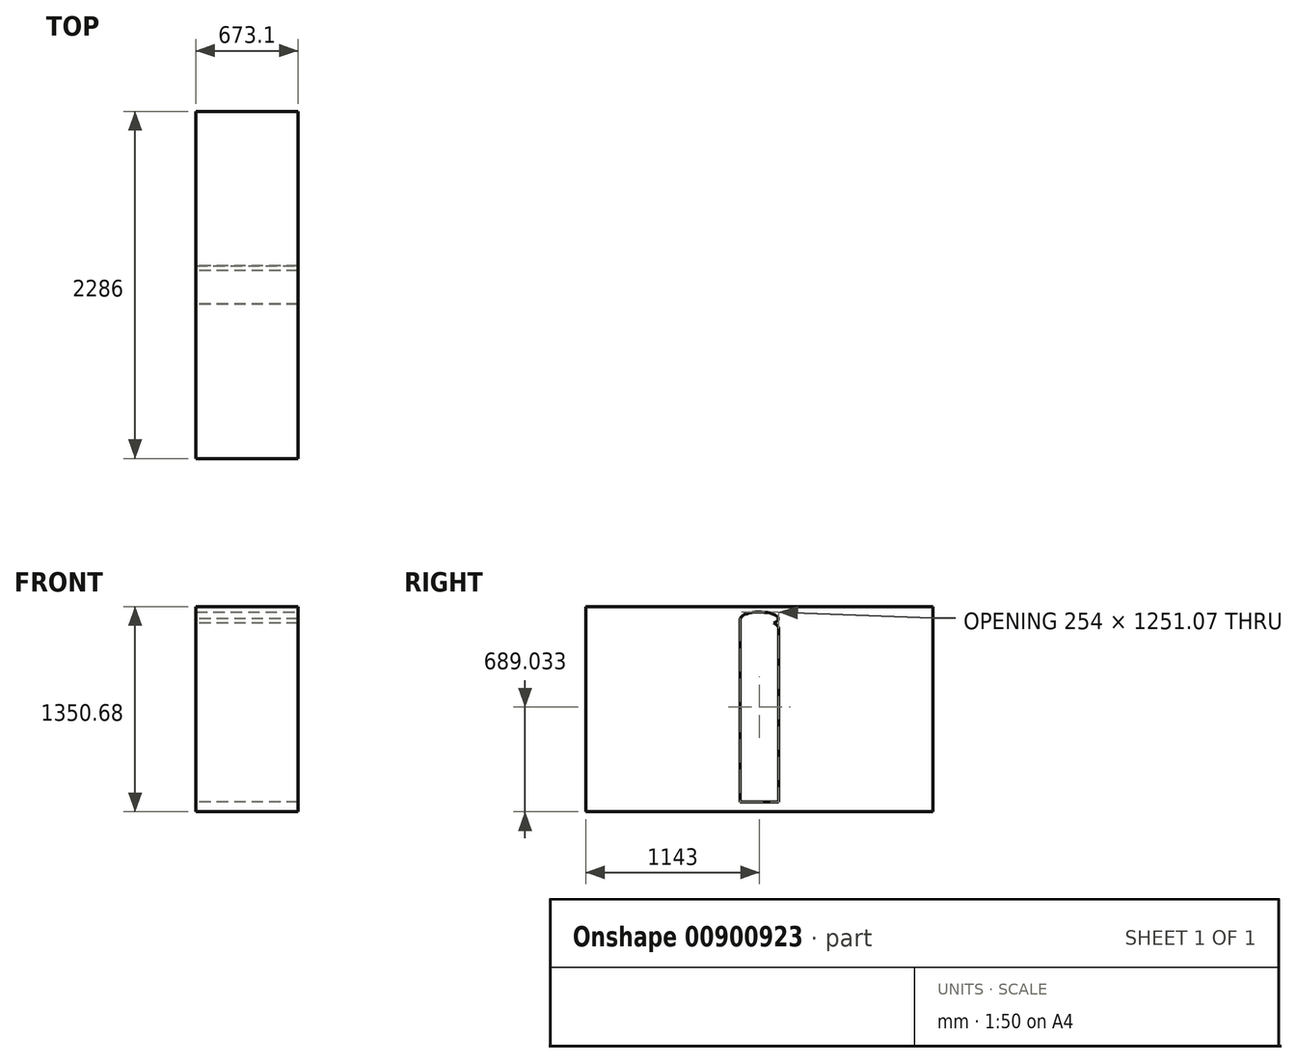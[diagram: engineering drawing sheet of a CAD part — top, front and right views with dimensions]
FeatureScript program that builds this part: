
annotation { "Feature Type Name" : "Feature", "Feature Type Description" : "" }
export const myFeature = defineFeature(function(context is Context, id is Id, definition is map)
    precondition{}
    {
        {
            var Q0;
            Q0=qCreatedBy(makeId("Right.planeOp"),FACE);
            var sketch = newSketch(context, id + "F0", { "sketchPlane" : qUnion([Q0])});
            skLineSegment(sketch, "E0.bottom", {"start": v(-1143, 635) * mm, "end": v(1143, 635) * mm});
            skLineSegment(sketch, "E0.top", {"start": v(-1143, -635) * mm, "end": v(1143, -635) * mm});
            skLineSegment(sketch, "E0.left", {"start": v(-1143, 635) * mm, "end": v(-1143, -635) * mm});
            skLineSegment(sketch, "E0.right", {"start": v(1143, 635) * mm, "end": v(1143, -635) * mm});
            skPoint(sketch, "E0.middle", {"position": v(0, 0) * mm});
            skLineSegment(sketch, "E1", {"start": v(-1143, 571.5) * mm, "end": v(1143, 571.5) * mm});
            skLineSegment(sketch, "E2", {"start": v(-1143, -571.5) * mm, "end": v(1143, -571.5) * mm});
            skLineSegment(sketch, "E3", {"start": v(-1143, -493.46) * mm, "end": v(-127, -493.46) * mm});
            skEllipse(sketch, "E4", {"center": v(0, 571.5) * mm, "majorRadius": 127 * mm, "minorRadius": 52.54 * mm, "majorAxis": v(-1, 0)});
            skLineSegment(sketch, "E5", {"start": v(-127, 571.5) * mm, "end": v(-127, -571.5) * mm});
            skLineSegment(sketch, "E6", {"start": v(127, 571.5) * mm, "end": v(127, -571.5) * mm});
            skLineSegment(sketch, "E7.trimOffspring", {"start": v(127, -493.46) * mm, "end": v(1143, -493.46) * mm});
            skLineSegment(sketch, "E8", {"start": v(-127, 571.5) * mm, "end": v(-127, 1225.93) * mm});
            skLineSegment(sketch, "E9", {"start": v(-1143, -581.12) * mm, "end": v(-1089.12, -635) * mm});
            skLineSegment(sketch, "E10", {"start": v(-1143, 635) * mm, "end": v(-1143, 715.68) * mm});
            skLineSegment(sketch, "E11", {"start": v(-1143, 715.68) * mm, "end": v(1143, 715.68) * mm});
            skLineSegment(sketch, "E12", {"start": v(1143, 715.68) * mm, "end": v(1143, 635) * mm});
            skEllipse(sketch, "E13", {"center": v(0, 635) * mm, "majorRadius": 124.87 * mm, "minorRadius": 44.95 * mm, "majorAxis": v(1, 0)});
            skSolve(sketch);
        }
        {
            var Q0;
            Q0 = qSketchRegion(id + "F0", true);
            extrude(context, id + "F1", {"entities" : qUnion([Q0]), "depth" : 673.1 * mm, "offsetDistance" : 25.4 * mm});
        }
    });
